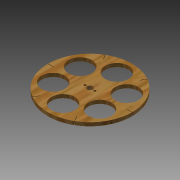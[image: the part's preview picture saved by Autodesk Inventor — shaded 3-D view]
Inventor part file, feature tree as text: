
AUTODESK INVENTOR PART (.ipt)
format: ipt  version: 2013 (Build 170138000, 138)  size: 154,112 bytes
history: native  units: in
note: dims shown in document units (in); Inventor stores cm internally (conversion verified against a paired STEP export)
features: sketch x3, extrude x2, hole x1, pattern_circular x1
ambient origin geometry x8: Origin, YZ Plane, XZ Plane, XY Plane, X Axis, Y Axis, Z Axis, Center Point
bodies: Solid1 (feature_tree)
feature tree (7):
  extrude  "Extrusion1"  Depth=1.9232in
  hole  "Hole1"  [1 undecoded]
  extrude  "Extrusion2"  Depth=0.25in TaperAngle=0.0deg
  pattern_circular  "Circular Pattern1"  [2 undecoded]
  sketch  "Sketch1"  dims[d0=1.6535in d2=1.9232in]
  sketch  "Sketch2"  dims[d3=2.3622in d5=360.0deg d7=6.0in]
  sketch  "Sketch3"  dims[d8=0.4in d9=0.25in d10=0.0in d11=0.7in d13=0.1695in d14=0.75in d15=0.375in d16=0.25in d17=0.5635in d18=1.0in d19=0.8108in d21=0.3937in d22=0.0394in d23=60.0deg d24=0.0in d25=0.0in d26=2.3622in d27=360.0deg d29=0.1in]
note: 3 required parameter values undecoded (feature->parameter linkage not recoverable at this tier; creation-order binding heuristic only, values carry confidence <= 0.55)
